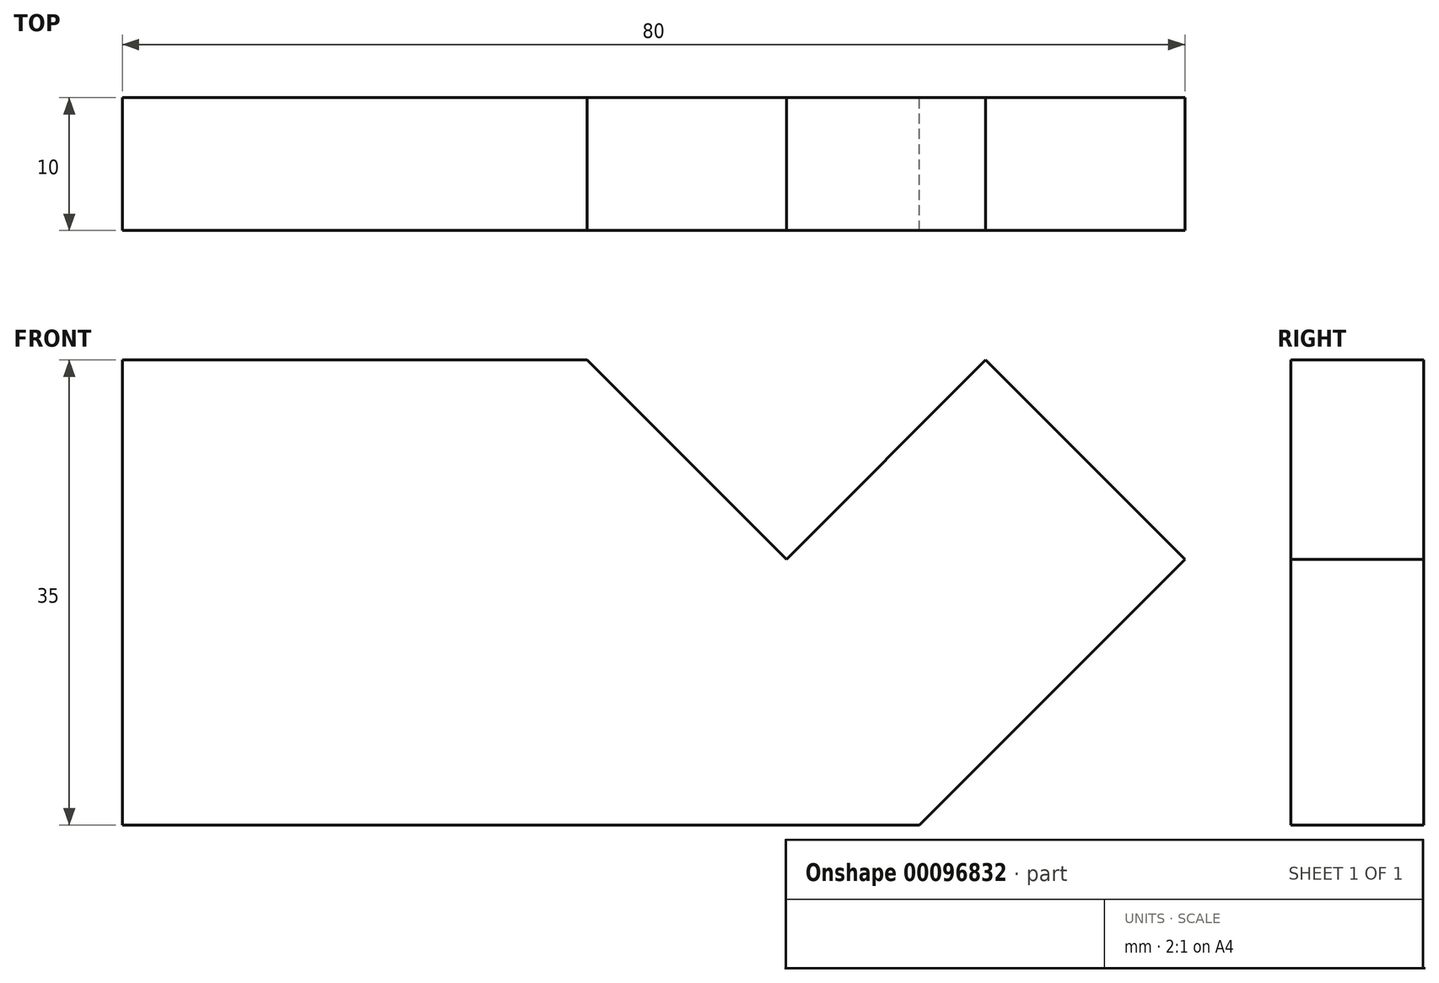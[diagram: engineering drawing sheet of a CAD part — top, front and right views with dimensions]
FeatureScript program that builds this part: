
annotation { "Feature Type Name" : "Feature", "Feature Type Description" : "" }
export const myFeature = defineFeature(function(context is Context, id is Id, definition is map)
    precondition{}
    {
        {
            var Q0;
            Q0=qCreatedBy(makeId("Front.planeOp"),FACE);
            var sketch = newSketch(context, id + "F0", { "sketchPlane" : qUnion([Q0])});
            skLineSegment(sketch, "E0", {"start": v(0, 0) * mm, "end": v(0, 35) * mm});
            skLineSegment(sketch, "E1", {"start": v(0, 0) * mm, "end": v(60, 0) * mm});
            skLineSegment(sketch, "E2", {"start": v(60, 0) * mm, "end": v(80, 20) * mm});
            skLineSegment(sketch, "E3", {"start": v(80, 20) * mm, "end": v(65, 35) * mm});
            skLineSegment(sketch, "E4", {"start": v(65, 35) * mm, "end": v(50, 20) * mm});
            skLineSegment(sketch, "E5", {"start": v(0, 35) * mm, "end": v(35, 35) * mm});
            skLineSegment(sketch, "E6", {"start": v(35, 35) * mm, "end": v(50, 20) * mm});
            skSolve(sketch);
        }
        {
            var Q0;
            Q0=makeQuery(id+"F0.imprint","IMPRINT",FACE,{"disambiguationData":[TD([[makeQuery(id+"F0.imprint","IMPRINT",EDGE,{"derivedFrom":sQuery(id+"F0.wireOp",EDGE,"E0")}),-1.0]])]});
            extrude(context, id + "F1", {"entities" : qUnion([Q0]), "endBound" : BoundingType.SYMMETRIC, "depth" : 10 * mm});
        }
    });
